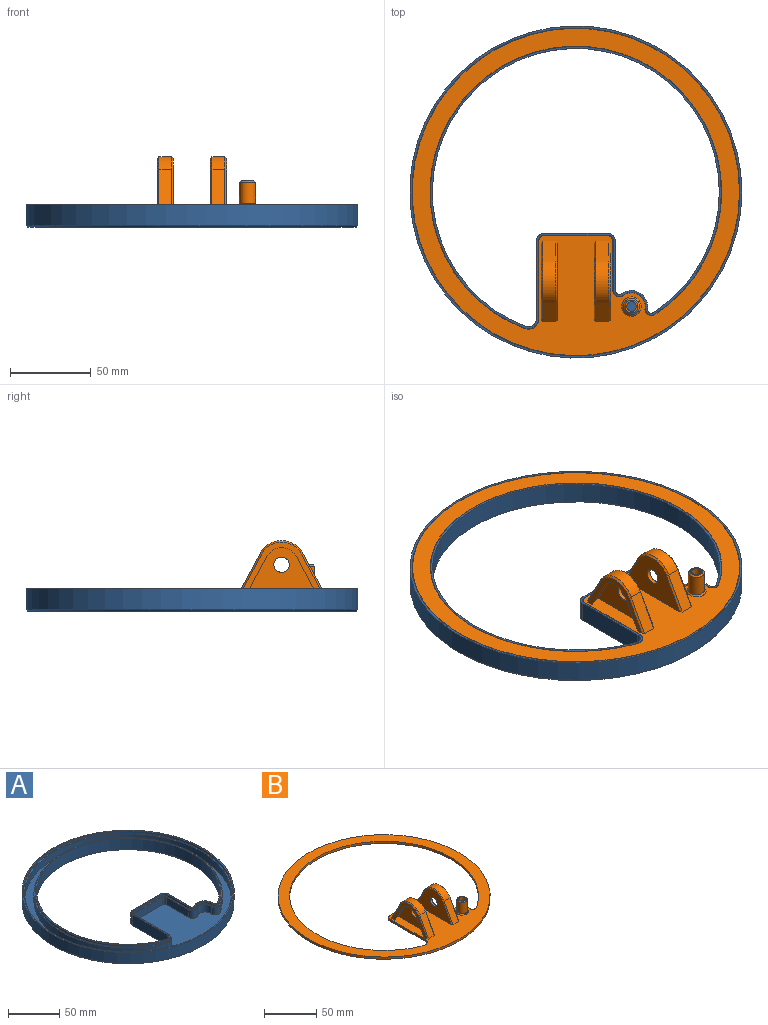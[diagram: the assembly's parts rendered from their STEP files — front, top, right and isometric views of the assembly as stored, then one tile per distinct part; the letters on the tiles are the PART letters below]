
ASSEMBLY  parts=2 mates=1
PART A: 50 faces, bbox 206x206x14 mm
  f0: plane 180.5x175.15mm, normal (0,0,1), area 822.3mm2, adj f1,f2,f3,f4,f5,f6,f7,f8
  f1: cylinder r=2.5mm len=13mm, axis (0,0,-1), area 72mm2, adj f0,f2,f11,f40
  f2: plane 30.51x13mm, normal (1,0,0), area 396.6mm2, adj f0,f1,f3,f39
  f3: cylinder r=5mm len=13mm, axis (0,0,-1), area 102.1mm2, adj f0,f2,f4,f41
  f4: plane 39x13mm, normal (0,1,0), area 507mm2, adj f0,f3,f5,f43
  f5: cylinder r=5mm len=13mm, axis (0,0,-1), area 102.1mm2, adj f0,f4,f6,f45
  f6: plane 48.09x13mm, normal (-1,0,0), area 625.1mm2, adj f0,f5,f7,f47
  f7: cylinder r=5mm len=13mm, axis (0,0,-1), area 125.4mm2, adj f0,f6,f8,f48
  f8: cylinder r=89mm len=178mm, axis (0,0,-1), area 6191.5mm2, adj f0,f7,f9,f46
  f9: cylinder r=2.5mm len=13mm, axis (0,0,-1), area 73.9mm2, adj f0,f8,f11,f44
  f10: cylinder r=103mm len=206mm, axis (0,0,-1), area 8413.2mm2, adj f12,f49
  f11: cylinder r=10mm len=16mm, axis (0,0,-1), area 304.7mm2, adj f0,f1,f9,f42
  f12: plane 206x206mm, normal (0,0,1), area 804.1mm2, adj f10,f25
  f13: plane 204x204mm, normal (0,0,-1), area 10581.9mm2, adj f39,f40,f41,f42,f43,f44,f45,f46
  f14: plane 183x177.65mm, normal (0,0,1), area 832.1mm2, adj f15,f16,f17,f18,f19,f20,f21,f22
  f15: cylinder r=6.25mm len=8.45mm, axis (0,0,1), area 30.2mm2, adj f0,f14,f16,f24
  f16: plane 48.09x2.5mm, normal (1,0,0), area 120.2mm2, adj f0,f14,f15,f17
  f17: cylinder r=3.75mm len=3.75mm, axis (0,0,1), area 14.7mm2, adj f0,f14,f16,f18
  f18: plane 39x2.5mm, normal (0,-1,0), area 97.5mm2, adj f0,f14,f17,f19
  f19: cylinder r=3.75mm len=3.75mm, axis (0,0,1), area 14.7mm2, adj f0,f14,f18,f20
  f20: plane 30.51x2.5mm, normal (-1,0,0), area 76.3mm2, adj f0,f14,f19,f21
  f21: cylinder r=3.75mm len=6mm, axis (0,0,1), area 20.8mm2, adj f0,f14,f20,f22
  f22: cylinder r=8.75mm len=14mm, axis (0,0,1), area 51.3mm2, adj f0,f14,f21,f23
  f23: cylinder r=3.75mm len=5.78mm, axis (0,0,1), area 21.3mm2, adj f0,f14,f22,f24
  f24: cylinder r=90.25mm len=180.5mm, axis (0,0,1), area 1207.4mm2, adj f0,f14,f15,f23
  f25: cylinder r=101.75mm len=203.5mm, axis (0,0,1), area 1598.3mm2, adj f12,f26
  f26: plane 203.5x203.5mm, normal (0,0,1), area 794.2mm2, adj f25,f27
  f27: cylinder r=100.5mm len=201mm, axis (0,0,-1), area 5683.1mm2, adj f26,f28
  f28: plane 201x201mm, normal (0,0,1), area 8630.3mm2, adj f27,f29,f30,f31,f32,f33,f34,f35
  f29: cylinder r=7.5mm len=12mm, axis (0,0,-1), area 158.2mm2, adj f14,f28,f30,f38
  f30: cylinder r=5mm len=9mm, axis (0,0,-1), area 102.3mm2, adj f14,f28,f29,f31
  f31: cylinder r=91.5mm len=183mm, axis (0,0,-1), area 4406.8mm2, adj f14,f28,f30,f32
  f32: cylinder r=7.5mm len=10.13mm, axis (0,0,-1), area 130.3mm2, adj f14,f28,f31,f33
  f33: plane 48.09x9mm, normal (1,0,0), area 432.8mm2, adj f14,f28,f32,f34
  f34: cylinder r=2.5mm len=9mm, axis (0,0,-1), area 35.3mm2, adj f14,f28,f33,f35
  f35: plane 39x9mm, normal (0,-1,0), area 351mm2, adj f14,f28,f34,f36
  f36: cylinder r=2.5mm len=9mm, axis (0,0,-1), area 35.3mm2, adj f14,f28,f35,f37
  f37: plane 30.51x9mm, normal (-1,0,0), area 274.6mm2, adj f14,f28,f36,f38
  f38: cylinder r=5mm len=9mm, axis (0,0,-1), area 99.6mm2, adj f14,f28,f29,f37
  f39: plane 30.51x1mm, normal (0.71,0,-0.71), area 43.1mm2, adj f2,f13,f40,f41
  f40: cone r=3.5mm half-angle=45deg, axis (0,0,-1), area 9.4mm2, adj f1,f13,f39,f42
  f41: cone r=5mm half-angle=45deg, axis (0,0,1), area 10mm2, adj f3,f13,f39,f43
  f42: cone r=10mm half-angle=45deg, axis (0,0,1), area 31.5mm2, adj f11,f13,f40,f44
  f43: plane 39x1mm, normal (0,0.71,-0.71), area 55.2mm2, adj f4,f13,f41,f45
  f44: cone r=3.5mm half-angle=45deg, axis (0,0,-1), area 9.6mm2, adj f9,f13,f42,f46
  f45: cone r=5mm half-angle=45deg, axis (0,0,1), area 10mm2, adj f5,f13,f43,f47
  f46: cone r=90mm half-angle=45deg, axis (0,0,-1), area 677.3mm2, adj f8,f13,f44,f48
  f47: plane 48.09x1mm, normal (-0.71,0,-0.71), area 68mm2, adj f6,f13,f45,f48
  f48: cone r=6mm half-angle=45deg, axis (0,0,-1), area 15mm2, adj f7,f13,f46,f47
  f49: cone r=103mm half-angle=45deg, axis (0,0,1), area 910.8mm2, adj f10,f13
PART B: 56 faces, bbox 203x203x32.5 mm
  f0: plane 47.73x29mm, normal (1,0,0), area 259.8mm2, adj f5,f37,f38,f39,f53,f54,f55
  f1: cylinder r=4.75mm len=9.5mm, axis (-1,0,0), area 74.6mm2, adj f2,f44
  f2: plane 47.73x29mm, normal (1,0,0), area 841.5mm2, adj f1,f5,f28,f29,f30
  f3: plane 47.73x29mm, normal (-1,0,0), area 259.8mm2, adj f5,f34,f35,f36,f46,f47,f48
  f4: plane 47.73x29mm, normal (-1,0,0), area 841.5mm2, adj f5,f24,f31,f32,f33
  f5: plane 203x203mm, normal (0,0,1), area 9478.4mm2, adj f0,f2,f3,f4,f6,f7,f8,f9
  f6: cylinder r=90.5mm len=181mm, axis (0,0,-1), area 1210.7mm2, adj f5,f7,f15,f17
  f7: cylinder r=4mm len=6.17mm, axis (0,0,-1), area 22.7mm2, adj f5,f6,f8,f17
  f8: cylinder r=8.5mm len=13.6mm, axis (0,0,-1), area 49.8mm2, adj f5,f7,f9,f17
  f9: cylinder r=4mm len=6.4mm, axis (0,0,-1), area 22.1mm2, adj f5,f8,f10,f17
  f10: plane 30.51x2.5mm, normal (1,0,0), area 76.3mm2, adj f5,f9,f11,f17
  f11: cylinder r=3.5mm len=3.5mm, axis (0,0,-1), area 13.7mm2, adj f5,f10,f12,f17
  f12: plane 39x2.5mm, normal (0,1,0), area 97.5mm2, adj f5,f11,f13,f17
  f13: cylinder r=3.5mm len=3.5mm, axis (0,0,-1), area 13.7mm2, adj f5,f12,f14,f17
  f14: plane 48.09x2.5mm, normal (-1,0,0), area 120.2mm2, adj f5,f13,f15,f17
  f15: cylinder r=6.5mm len=8.78mm, axis (0,0,-1), area 31.4mm2, adj f5,f6,f14,f17
  f16: cylinder r=101.5mm len=203mm, axis (0,0,-1), area 1594.4mm2, adj f5,f17
  f17: plane 203x203mm, normal (0,0,-1), area 9903.1mm2, adj f6,f7,f8,f9,f10,f11,f12,f13
  f18: cylinder r=5mm len=13mm, axis (0,0,-1), area 408.4mm2, adj f40,f41
  f19: plane 8x8mm, normal (0,0,1), area 22mm2, adj f27,f41
  f20: cylinder r=15mm len=26.47mm, axis (-1,0,0), area 259.4mm2, adj f21,f25,f32,f38
  f21: plane 22.06x11.76mm, normal (0,-0.88,0.47), area 200mm2, adj f5,f20,f31,f37
  f22: plane 22.06x11.76mm, normal (0,-0.88,0.47), area 200mm2, adj f5,f23,f28,f36
  f23: cylinder r=15mm len=26.47mm, axis (-1,0,0), area 259.4mm2, adj f22,f26,f29,f35
  f24: cylinder r=4.75mm len=9.5mm, axis (-1,0,0), area 74.6mm2, adj f4,f51
  f25: plane 22.06x11.76mm, normal (0,0.88,0.47), area 200mm2, adj f5,f20,f33,f39
  f26: plane 22.06x11.76mm, normal (0,0.88,0.47), area 200mm2, adj f5,f23,f30,f34
  f27: cylinder r=3mm len=17.5mm, axis (0,0,1), area 329.9mm2, adj f17,f19
  f28: plane 22.06x12.65mm, normal (0.71,-0.62,0.33), area 35mm2, adj f2,f5,f22,f29
  f29: cone r=14mm half-angle=45deg, axis (-1,0,0), area 44.3mm2, adj f2,f23,f28,f30
  f30: plane 22.06x12.65mm, normal (0.71,0.62,0.33), area 35mm2, adj f2,f5,f26,f29
  f31: plane 22.06x12.65mm, normal (-0.71,-0.62,0.33), area 35mm2, adj f4,f5,f21,f32
  f32: cone r=15mm half-angle=45deg, axis (1,0,0), area 44.3mm2, adj f4,f20,f31,f33
  f33: plane 22.06x12.65mm, normal (-0.71,0.62,0.33), area 35mm2, adj f4,f5,f25,f32
  f34: plane 22.06x12.65mm, normal (-0.71,0.62,0.33), area 35mm2, adj f3,f5,f26,f35
  f35: cone r=14mm half-angle=45deg, axis (1,0,0), area 44.3mm2, adj f3,f23,f34,f36
  f36: plane 22.06x12.65mm, normal (-0.71,-0.62,0.33), area 35mm2, adj f3,f5,f22,f35
  f37: plane 22.06x12.65mm, normal (0.71,-0.62,0.33), area 35mm2, adj f0,f5,f21,f38
  f38: cone r=14mm half-angle=45deg, axis (-1,0,0), area 44.3mm2, adj f0,f20,f37,f39
  f39: plane 22.06x12.65mm, normal (0.71,0.62,0.33), area 35mm2, adj f0,f5,f25,f38
  f40: cone r=5mm half-angle=45deg, axis (0,0,-1), area 48.9mm2, adj f5,f18
  f41: cone r=4mm half-angle=45deg, axis (0,0,-1), area 40mm2, adj f18,f19
  f42: plane 20.88x11.14mm, normal (0,0.88,-0.47), area 129.3mm2, adj f5,f44,f45,f48
  f43: plane 20.88x11.14mm, normal (0,-0.88,-0.47), area 129.3mm2, adj f5,f44,f45,f46
  f44: plane 44.33x27.5mm, normal (-1,0,0), area 726.3mm2, adj f1,f5,f42,f43,f45
  f45: cylinder r=12.5mm len=22.06mm, axis (-1,0,0), area 147.7mm2, adj f42,f43,f44,f47
  f46: plane 20.88x12.93mm, normal (0.71,-0.62,-0.33), area 66.6mm2, adj f3,f5,f43,f47
  f47: cone r=12.23mm half-angle=45deg, axis (1,0,0), area 71.5mm2, adj f3,f45,f46,f48
  f48: plane 20.88x12.93mm, normal (0.71,0.62,-0.33), area 66.6mm2, adj f3,f5,f42,f47
  f49: plane 20.88x11.14mm, normal (0,0.88,-0.47), area 129.3mm2, adj f5,f51,f52,f53
  f50: plane 20.88x11.14mm, normal (0,-0.88,-0.47), area 129.3mm2, adj f5,f51,f52,f55
  f51: plane 44.33x27.5mm, normal (1,0,0), area 726.3mm2, adj f5,f24,f49,f50,f52
  f52: cylinder r=12.5mm len=22.06mm, axis (-1,0,0), area 147.7mm2, adj f49,f50,f51,f54
  f53: plane 20.88x12.93mm, normal (-0.71,0.62,-0.33), area 66.6mm2, adj f0,f5,f49,f54
  f54: cone r=12.23mm half-angle=45deg, axis (-1,0,0), area 71.5mm2, adj f0,f52,f53,f55
  f55: plane 20.88x12.93mm, normal (-0.71,-0.62,-0.33), area 66.6mm2, adj f0,f5,f50,f54
PLACE A t=(0,0,86)mm
PLACE B t=(0,0,-2.5)mm
MATE fastened A.f5 <-> B.f13  axis (0,0,1) through (-19.5,-30.56,97.5)mm
